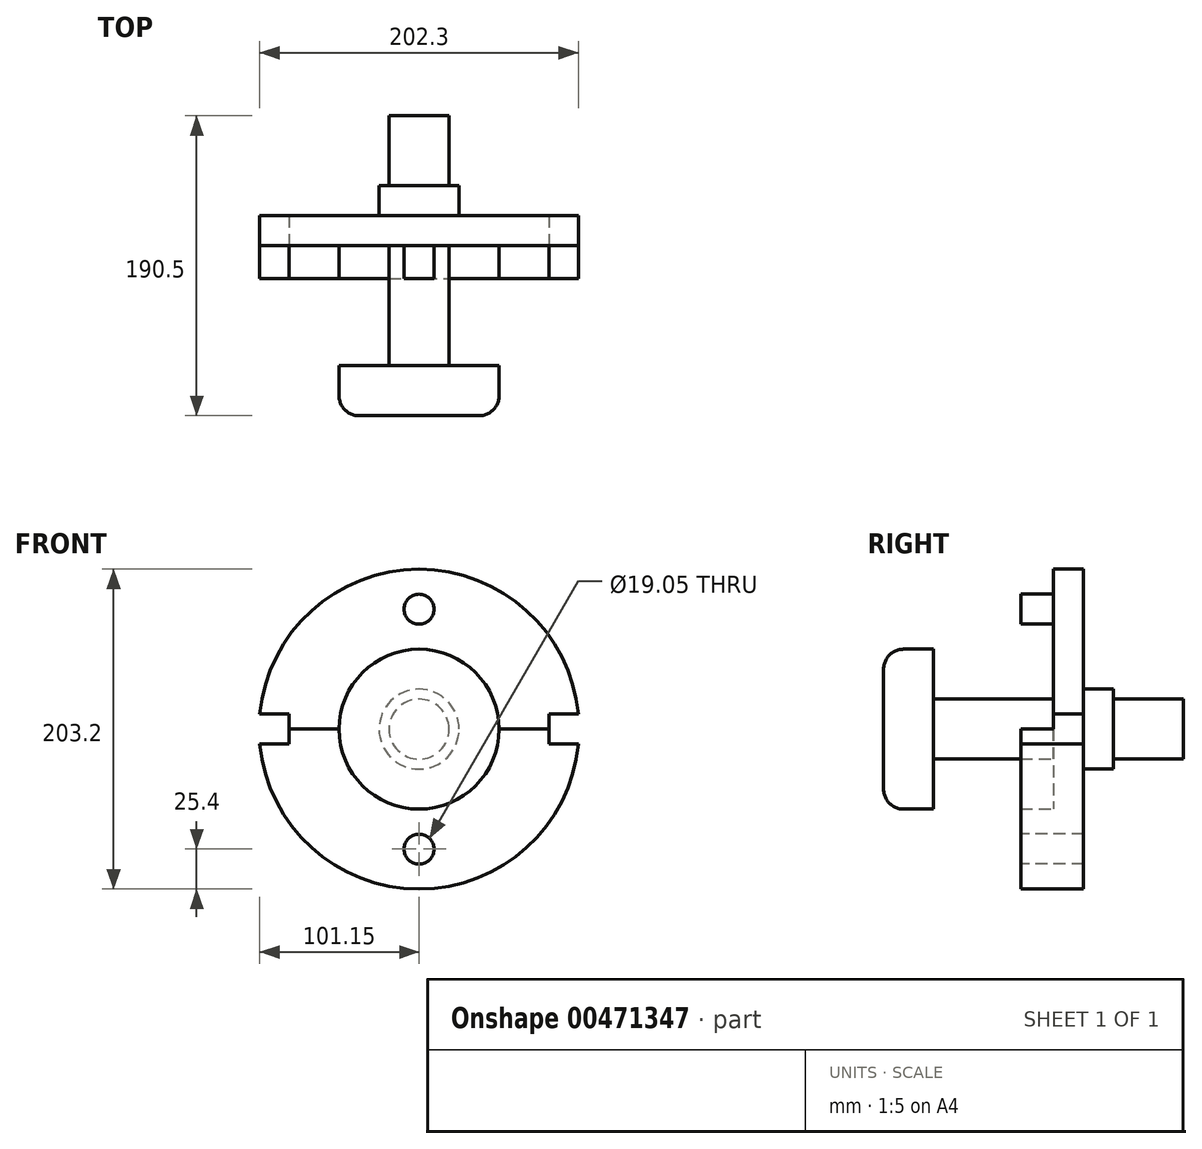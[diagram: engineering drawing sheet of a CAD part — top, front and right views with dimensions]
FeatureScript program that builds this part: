
annotation { "Feature Type Name" : "Feature", "Feature Type Description" : "" }
export const myFeature = defineFeature(function(context is Context, id is Id, definition is map)
    precondition{}
    {
        {
            var Q0;
            Q0=qCreatedBy(makeId("Front.planeOp"),FACE);
            var sketch = newSketch(context, id + "F0", { "sketchPlane" : qUnion([Q0])});
            skCircle(sketch, "E0", {"center": v(0, 0) * mm, "radius": 101.6 * mm});
            skCircle(sketch, "E1", {"center": v(0, 0) * mm, "radius": 76.2 * mm});
            skCircle(sketch, "E2", {"center": v(0, 0) * mm, "radius": 50.8 * mm});
            skCircle(sketch, "E3", {"center": v(0, 0) * mm, "radius": 19.05 * mm});
            skLineSegment(sketch, "E4", {"start": v(0, 0) * mm, "end": v(82.55, 0) * mm});
            skLineSegment(sketch, "E5", {"start": v(82.55, 0) * mm, "end": v(82.55, -9.53) * mm});
            skLineSegment(sketch, "E6", {"start": v(82.55, -9.53) * mm, "end": v(101.15, -9.53) * mm});
            skLineSegment(sketch, "E7", {"start": v(82.55, 0) * mm, "end": v(82.55, 9.53) * mm});
            skLineSegment(sketch, "E8", {"start": v(82.55, 9.53) * mm, "end": v(101.15, 9.53) * mm});
            skLineSegment(sketch, "E9", {"start": v(0, 0) * mm, "end": v(-82.55, 0) * mm});
            skLineSegment(sketch, "E10", {"start": v(-82.55, 0) * mm, "end": v(-82.55, -9.53) * mm});
            skLineSegment(sketch, "E11", {"start": v(-82.55, -9.53) * mm, "end": v(-101.15, -9.53) * mm});
            skLineSegment(sketch, "E12", {"start": v(-82.55, 0) * mm, "end": v(-82.55, 9.52) * mm});
            skLineSegment(sketch, "E13", {"start": v(-82.55, 9.52) * mm, "end": v(-101.15, 9.52) * mm});
            skCircle(sketch, "E14", {"center": v(0, 76.2) * mm, "radius": 9.53 * mm});
            skCircle(sketch, "E15", {"center": v(0, -76.2) * mm, "radius": 9.53 * mm});
            skCircle(sketch, "E16", {"center": v(0, 0) * mm, "radius": 25.4 * mm});
            skSolve(sketch);
        }
        {
            var Q0;
            {var subQ0=sQuery(id+"F0.wireOp",EDGE,"E7");Q0=makeQuery(id+"F0.imprint","IMPRINT",FACE,{"disambiguationData":[TD([[makeQuery(id+"F0.imprint","IMPRINT",EDGE,{"derivedFrom":subQ0}),1.0]])]});}
            var Q1;
            {var subQ5=sQuery(id+"F0.wireOp",EDGE,"E5");Q1=makeQuery(id+"F0.imprint","IMPRINT",FACE,{"disambiguationData":[TD([[makeQuery(id+"F0.imprint","IMPRINT",EDGE,{"derivedFrom":subQ5}),-1.0]])]});}
            var Q2;
            {var subQ1=sQuery(id+"F0.wireOp",EDGE,"E1");var subQ5=sQuery(id+"F0.wireOp",EDGE,"E9");var subQ9=makeQuery(id+"F0.imprint","INTERSECT",VERTEX,{"derivedFrom":[subQ1,subQ5]});Q2=makeQuery(id+"F0.imprint","IMPRINT",FACE,{"disambiguationData":[TD([[makeQuery(id+"F0.imprint","IMPRINT",EDGE,{"disambiguationData":[TD([[subQ9,-1.0]])],"derivedFrom":subQ1}),1.0]])]});}
            var Q3;
            {var subQ0=sQuery(id+"F0.wireOp",EDGE,"E4");var subQ1=sQuery(id+"F0.wireOp",EDGE,"E2");var subQ2=makeQuery(id+"F0.imprint","INTERSECT",VERTEX,{"derivedFrom":[subQ1,subQ0]});Q3=makeQuery(id+"F0.imprint","IMPRINT",FACE,{"disambiguationData":[TD([[makeQuery(id+"F0.imprint","IMPRINT",EDGE,{"disambiguationData":[TD([[subQ2,1.0]])],"derivedFrom":subQ1}),1.0]])]});}
            var Q4;
            {var subQ0=sQuery(id+"F0.wireOp",EDGE,"E4");var subQ1=sQuery(id+"F0.wireOp",EDGE,"E2");var subQ2=makeQuery(id+"F0.imprint","INTERSECT",VERTEX,{"derivedFrom":[subQ1,subQ0]});Q4=makeQuery(id+"F0.imprint","IMPRINT",FACE,{"disambiguationData":[TD([[makeQuery(id+"F0.imprint","IMPRINT",EDGE,{"disambiguationData":[TD([[subQ2,-1.0]])],"derivedFrom":subQ1}),1.0]])]});}
            var Q5;
            {var subQ5=sQuery(id+"F0.wireOp",EDGE,"E1");var subQ7=sQuery(id+"F0.wireOp",EDGE,"E14");var subQ10=makeQuery(id+"F0.imprint","INTERSECT",VERTEX,{"disambiguationData":[OD(0.0)],"derivedFrom":[subQ5,subQ7]});Q5=makeQuery(id+"F0.imprint","IMPRINT",FACE,{"disambiguationData":[TD([[makeQuery(id+"F0.imprint","IMPRINT",EDGE,{"disambiguationData":[TD([[subQ10,1.0]])],"derivedFrom":subQ5}),1.0]])]});}
            var Q6;
            {var subQ0=sQuery(id+"F0.wireOp",EDGE,"E4");var subQ1=sQuery(id+"F0.wireOp",EDGE,"E3");var subQ2=makeQuery(id+"F0.imprint","INTERSECT",VERTEX,{"derivedFrom":[subQ1,subQ0]});Q6=makeQuery(id+"F0.imprint","IMPRINT",FACE,{"disambiguationData":[TD([[makeQuery(id+"F0.imprint","IMPRINT",EDGE,{"disambiguationData":[TD([[subQ2,1.0]])],"derivedFrom":subQ1}),1.0]])]});}
            var Q7;
            {var subQ0=sQuery(id+"F0.wireOp",EDGE,"E4");var subQ1=sQuery(id+"F0.wireOp",EDGE,"E3");var subQ2=makeQuery(id+"F0.imprint","INTERSECT",VERTEX,{"derivedFrom":[subQ1,subQ0]});Q7=makeQuery(id+"F0.imprint","IMPRINT",FACE,{"disambiguationData":[TD([[makeQuery(id+"F0.imprint","IMPRINT",EDGE,{"disambiguationData":[TD([[subQ2,1.0]])],"derivedFrom":subQ1}),1.0]])]});}
            var Q8;
            {var subQ0=sQuery(id+"F0.wireOp",EDGE,"E4");var subQ1=sQuery(id+"F0.wireOp",EDGE,"E3");var subQ2=makeQuery(id+"F0.imprint","INTERSECT",VERTEX,{"derivedFrom":[subQ1,subQ0]});Q8=makeQuery(id+"F0.imprint","IMPRINT",FACE,{"disambiguationData":[TD([[makeQuery(id+"F0.imprint","IMPRINT",EDGE,{"disambiguationData":[TD([[subQ2,-1.0]])],"derivedFrom":subQ1}),1.0]])]});}
            var Q9;
            {var subQ0=sQuery(id+"F0.wireOp",EDGE,"E15");var subQ1=sQuery(id+"F0.wireOp",EDGE,"E1");var subQ2=makeQuery(id+"F0.imprint","INTERSECT",VERTEX,{"disambiguationData":[OD(0.0)],"derivedFrom":[subQ1,subQ0]});Q9=makeQuery(id+"F0.imprint","IMPRINT",FACE,{"disambiguationData":[TD([[makeQuery(id+"F0.imprint","IMPRINT",EDGE,{"disambiguationData":[TD([[subQ2,-1.0]])],"derivedFrom":subQ1}),-1.0]])]});}
            var Q10;
            {var subQ0=sQuery(id+"F0.wireOp",EDGE,"E14");var subQ1=sQuery(id+"F0.wireOp",EDGE,"E1");var subQ2=makeQuery(id+"F0.imprint","INTERSECT",VERTEX,{"disambiguationData":[OD(0.0)],"derivedFrom":[subQ1,subQ0]});Q10=makeQuery(id+"F0.imprint","IMPRINT",FACE,{"disambiguationData":[TD([[makeQuery(id+"F0.imprint","IMPRINT",EDGE,{"disambiguationData":[TD([[subQ2,-1.0]])],"derivedFrom":subQ1}),1.0]])]});}
            var Q11;
            {var subQ0=sQuery(id+"F0.wireOp",EDGE,"E14");var subQ1=sQuery(id+"F0.wireOp",EDGE,"E1");var subQ2=makeQuery(id+"F0.imprint","INTERSECT",VERTEX,{"disambiguationData":[OD(0.0)],"derivedFrom":[subQ1,subQ0]});Q11=makeQuery(id+"F0.imprint","IMPRINT",FACE,{"disambiguationData":[TD([[makeQuery(id+"F0.imprint","IMPRINT",EDGE,{"disambiguationData":[TD([[subQ2,-1.0]])],"derivedFrom":subQ1}),-1.0]])]});}
            var Q12;
            {var subQ0=sQuery(id+"F0.wireOp",EDGE,"E15");var subQ1=sQuery(id+"F0.wireOp",EDGE,"E1");var subQ2=makeQuery(id+"F0.imprint","INTERSECT",VERTEX,{"disambiguationData":[OD(0.0)],"derivedFrom":[subQ1,subQ0]});Q12=makeQuery(id+"F0.imprint","IMPRINT",FACE,{"disambiguationData":[TD([[makeQuery(id+"F0.imprint","IMPRINT",EDGE,{"disambiguationData":[TD([[subQ2,-1.0]])],"derivedFrom":subQ1}),1.0]])]});}
            var Q13;
            {var subQ0=sQuery(id+"F0.wireOp",EDGE,"E4");var subQ1=sQuery(id+"F0.wireOp",EDGE,"E3");var subQ2=makeQuery(id+"F0.imprint","INTERSECT",VERTEX,{"derivedFrom":[subQ1,subQ0]});Q13=makeQuery(id+"F0.imprint","IMPRINT",FACE,{"disambiguationData":[TD([[makeQuery(id+"F0.imprint","IMPRINT",EDGE,{"disambiguationData":[TD([[subQ2,1.0]])],"derivedFrom":subQ1}),-1.0]])]});}
            var Q14;
            {var subQ0=sQuery(id+"F0.wireOp",EDGE,"E4");var subQ1=sQuery(id+"F0.wireOp",EDGE,"E3");var subQ2=makeQuery(id+"F0.imprint","INTERSECT",VERTEX,{"derivedFrom":[subQ1,subQ0]});Q14=makeQuery(id+"F0.imprint","IMPRINT",FACE,{"disambiguationData":[TD([[makeQuery(id+"F0.imprint","IMPRINT",EDGE,{"disambiguationData":[TD([[subQ2,-1.0]])],"derivedFrom":subQ1}),-1.0]])]});}
            extrude(context, id + "F1", {"entities" : qUnion([Q0, Q1, Q2, Q3, Q4, Q5, Q6, Q7, Q8, Q9, Q10, Q11, Q12, Q13, Q14]), "oppositeDirection" : true, "depth" : 19.05 * mm});
        }
        {
            var Q0;
            {var subQ0=sQuery(id+"F0.wireOp",EDGE,"E4");var subQ1=sQuery(id+"F0.wireOp",EDGE,"E3");var subQ2=makeQuery(id+"F0.imprint","INTERSECT",VERTEX,{"derivedFrom":[subQ1,subQ0]});Q0=makeQuery(id+"F0.imprint","IMPRINT",FACE,{"disambiguationData":[TD([[makeQuery(id+"F0.imprint","IMPRINT",EDGE,{"disambiguationData":[TD([[subQ2,-1.0]])],"derivedFrom":subQ1}),1.0]])]});}
            var Q1;
            {var subQ0=sQuery(id+"F0.wireOp",EDGE,"E4");var subQ1=sQuery(id+"F0.wireOp",EDGE,"E3");var subQ2=makeQuery(id+"F0.imprint","INTERSECT",VERTEX,{"derivedFrom":[subQ1,subQ0]});Q1=makeQuery(id+"F0.imprint","IMPRINT",FACE,{"disambiguationData":[TD([[makeQuery(id+"F0.imprint","IMPRINT",EDGE,{"disambiguationData":[TD([[subQ2,1.0]])],"derivedFrom":subQ1}),1.0]])]});}
            extrude(context, id + "F2", {"entities" : qUnion([Q0, Q1]), "operationType" : NewBodyOperationType.ADD, "depth" : 76.2 * mm});
        }
        {
            var Q0;
            {var subQ0=sQuery(id+"F0.wireOp",EDGE,"E15");var subQ1=sQuery(id+"F0.wireOp",EDGE,"E1");var subQ2=makeQuery(id+"F0.imprint","INTERSECT",VERTEX,{"disambiguationData":[OD(0.0)],"derivedFrom":[subQ1,subQ0]});Q0=makeQuery(id+"F0.imprint","IMPRINT",FACE,{"disambiguationData":[TD([[makeQuery(id+"F0.imprint","IMPRINT",EDGE,{"disambiguationData":[TD([[subQ2,-1.0]])],"derivedFrom":subQ1}),1.0]])]});}
            var Q1;
            {var subQ0=sQuery(id+"F0.wireOp",EDGE,"E15");var subQ1=sQuery(id+"F0.wireOp",EDGE,"E1");var subQ2=makeQuery(id+"F0.imprint","INTERSECT",VERTEX,{"disambiguationData":[OD(0.0)],"derivedFrom":[subQ1,subQ0]});Q1=makeQuery(id+"F0.imprint","IMPRINT",FACE,{"disambiguationData":[TD([[makeQuery(id+"F0.imprint","IMPRINT",EDGE,{"disambiguationData":[TD([[subQ2,-1.0]])],"derivedFrom":subQ1}),-1.0]])]});}
            var Q2;
            {var subQ0=sQuery(id+"F0.wireOp",EDGE,"E14");var subQ1=sQuery(id+"F0.wireOp",EDGE,"E1");var subQ2=makeQuery(id+"F0.imprint","INTERSECT",VERTEX,{"disambiguationData":[OD(0.0)],"derivedFrom":[subQ1,subQ0]});Q2=makeQuery(id+"F0.imprint","IMPRINT",FACE,{"disambiguationData":[TD([[makeQuery(id+"F0.imprint","IMPRINT",EDGE,{"disambiguationData":[TD([[subQ2,-1.0]])],"derivedFrom":subQ1}),1.0]])]});}
            var Q3;
            {var subQ0=sQuery(id+"F0.wireOp",EDGE,"E14");var subQ1=sQuery(id+"F0.wireOp",EDGE,"E1");var subQ2=makeQuery(id+"F0.imprint","INTERSECT",VERTEX,{"disambiguationData":[OD(0.0)],"derivedFrom":[subQ1,subQ0]});Q3=makeQuery(id+"F0.imprint","IMPRINT",FACE,{"disambiguationData":[TD([[makeQuery(id+"F0.imprint","IMPRINT",EDGE,{"disambiguationData":[TD([[subQ2,-1.0]])],"derivedFrom":subQ1}),-1.0]])]});}
            extrude(context, id + "F3", {"entities" : qUnion([Q0, Q1, Q2, Q3]), "operationType" : NewBodyOperationType.ADD, "depth" : 20.83 * mm});
        }
        {
            var Q0;
            {var subQ0=sQuery(id+"F0.wireOp",EDGE,"E4");var subQ1=sQuery(id+"F0.wireOp",EDGE,"E3");var subQ2=makeQuery(id+"F0.imprint","INTERSECT",VERTEX,{"derivedFrom":[subQ1,subQ0]});Q0=makeQuery(id+"F0.imprint","IMPRINT",FACE,{"disambiguationData":[TD([[makeQuery(id+"F0.imprint","IMPRINT",EDGE,{"disambiguationData":[TD([[subQ2,-1.0]])],"derivedFrom":subQ1}),-1.0]])]});}
            var Q1;
            {var subQ0=sQuery(id+"F0.wireOp",EDGE,"E4");var subQ1=sQuery(id+"F0.wireOp",EDGE,"E3");var subQ2=makeQuery(id+"F0.imprint","INTERSECT",VERTEX,{"derivedFrom":[subQ1,subQ0]});Q1=makeQuery(id+"F0.imprint","IMPRINT",FACE,{"disambiguationData":[TD([[makeQuery(id+"F0.imprint","IMPRINT",EDGE,{"disambiguationData":[TD([[subQ2,1.0]])],"derivedFrom":subQ1}),-1.0]])]});}
            extrude(context, id + "F4", {"entities" : qUnion([Q0, Q1]), "operationType" : NewBodyOperationType.ADD, "oppositeDirection" : true, "depth" : 38.1 * mm});
        }
        {
            var Q0;
            Q0=makeQuery(id+"F4.boolean.opBoolean","SPLIT",FACE,{"disambiguationData":[TD([makeQuery(id+"F4.opExtrude","SWEPT_FACE",FACE,{"disambiguationData":[OSD([sQuery(id+"F0.wireOp",EDGE,"E3")])]})])],"derivedFrom":makeQuery(id+"F1.opExtrude","CAP_FACE",FACE,{"disambiguationData":[OSD([sQuery(id+"F0.wireOp",EDGE,"E0"),sQuery(id+"F0.wireOp",EDGE,"E5"),sQuery(id+"F0.wireOp",EDGE,"E6"),sQuery(id+"F0.wireOp",EDGE,"E7"),sQuery(id+"F0.wireOp",EDGE,"E8"),sQuery(id+"F0.wireOp",EDGE,"E10"),sQuery(id+"F0.wireOp",EDGE,"E11"),sQuery(id+"F0.wireOp",EDGE,"E12"),sQuery(id+"F0.wireOp",EDGE,"E13")])],"isStart":false})});
            extrude(context, id + "F5", {"entities" : qUnion([Q0]), "operationType" : NewBodyOperationType.ADD, "depth" : 63.5 * mm});
        }
        {
            var Q0;
            Q0=makeQuery(id+"F2.opExtrude","CAP_FACE",FACE,{"disambiguationData":[OSD([sQuery(id+"F0.wireOp",EDGE,"E3")])],"isStart":false});
            var sketch = newSketch(context, id + "F6", { "sketchPlane" : qUnion([Q0])});
            skCircle(sketch, "E17", {"center": v(0, 0) * mm, "radius": 50.8 * mm});
            skSolve(sketch);
        }
        {
            var Q0;
            Q0=makeQuery(id+"F6.imprint","IMPRINT",FACE,{"disambiguationData":[TD([[makeQuery(id+"F6.imprint","IMPRINT",EDGE,{"derivedFrom":sQuery(id+"F6.wireOp",EDGE,"E17")}),1.0]])]});
            var Q1;
            Q1=makeQuery(id+"F6.imprint","IMPRINT",FACE,{"disambiguationData":[TD([[makeQuery(id+"F6.imprint","IMPRINT",EDGE,{"derivedFrom":makeQuery(id+"F2.opExtrude","CAP_EDGE",EDGE,{"disambiguationData":[OSD([sQuery(id+"F0.wireOp",EDGE,"E3")])],"isStart":false})}),1.0]])]});
            extrude(context, id + "F7", {"entities" : qUnion([Q0, Q1]), "operationType" : NewBodyOperationType.ADD, "depth" : 31.75 * mm});
        }
        {
            var Q0;
            Q0=makeQuery(id+"F7.opExtrude","CAP_EDGE",EDGE,{"disambiguationData":[OSD([sQuery(id+"F6.wireOp",EDGE,"E17")])],"isStart":false});
            fillet(context, id + "F8", {"entities" : qUnion([Q0]), "radius" : 12.7 * mm, "tangentPropagation" : true, "allowEdgeOverflow" : false});
        }
    });
